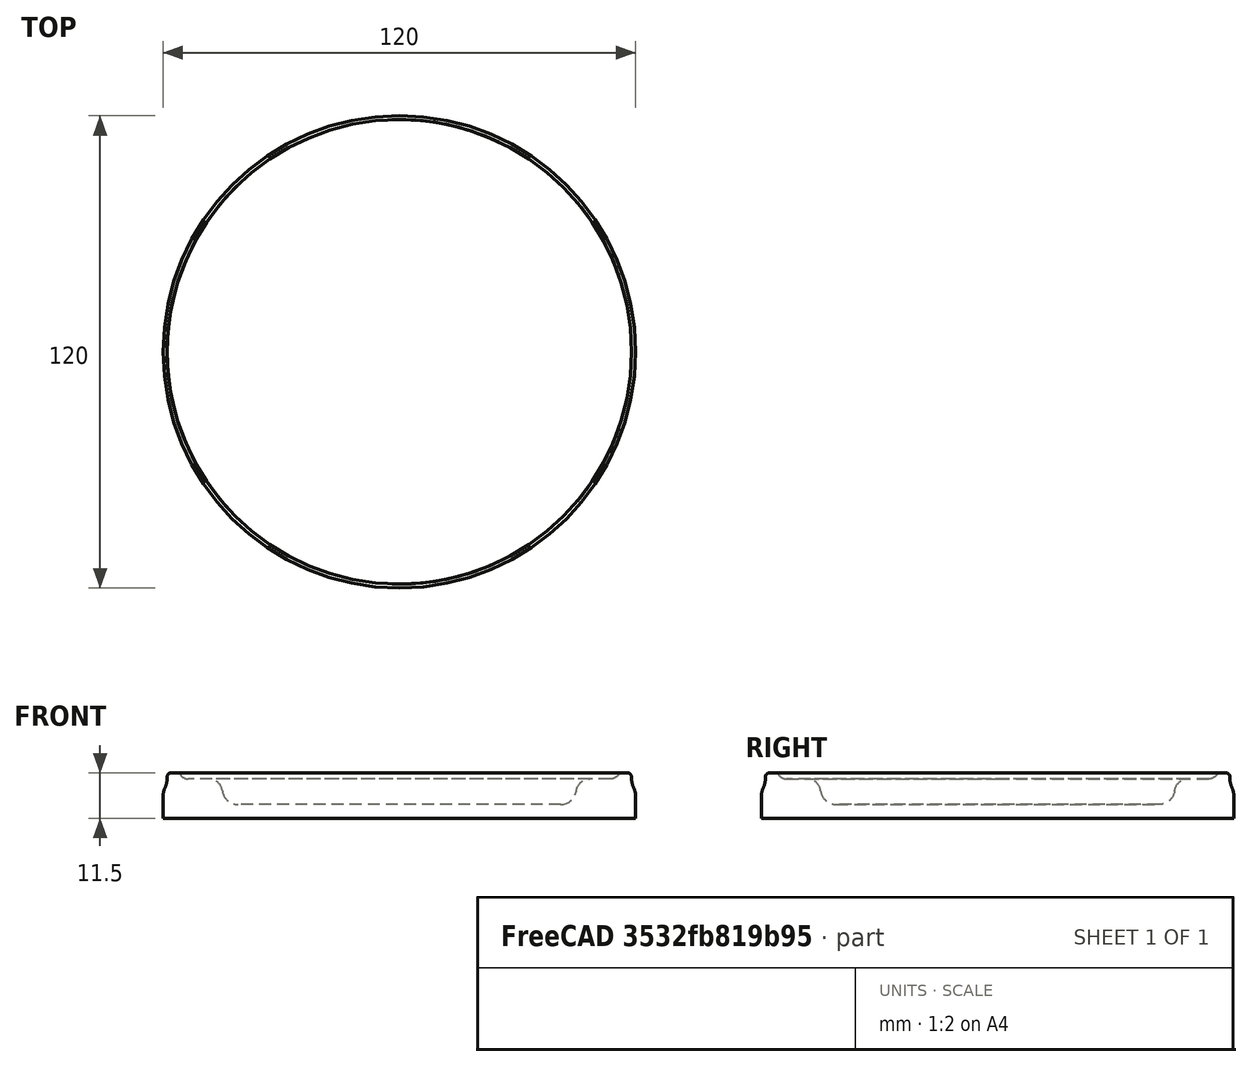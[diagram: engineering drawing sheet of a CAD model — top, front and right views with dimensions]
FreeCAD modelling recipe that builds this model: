
FCSTD DOCUMENT  (FreeCAD 0.16R)
Label: posavasos2017
License: All rights reserved
LicenseURL: http://en.wikipedia.org/wiki/All_rights_reserved
objects: Part::Fillet×6, Part::Cylinder×4, Part::Cut×2, Part::MultiFuse×1
note: 13 computed .brp shape members not serialized (recipe doc carries the construction recipe); baked Part::Feature solids carry a one-line shape summary decoded from their .brp

FEATURE [Part::Cylinder] Cylinder  label="Cilindro"
  Angle = 360
  Height = 30
  Placement = pos=(0,0,3.5) rot=(0,0,1;0rad)
  Radius = 45
FEATURE [Part::Cylinder] Cylinder001  label="Cilindro001"
  Angle = 360
  Height = 10
  Radius = 60
FEATURE [Part::Cut] Cut
  Base = -> Cylinder001
  Tool = -> Cylinder
FEATURE [Part::Fillet] Fillet
  Base = -> Cut
  Edges = 1 edges r=4: [Edge6]
FEATURE [Part::Fillet] Fillet001
  Base = -> Fillet
  Edges = 1 edges r=3.5: [Edge3]
FEATURE [Part::Fillet] Fillet002
  Base = -> Fillet001
  Edges = 1 edges r=4.2: [Edge6]
FEATURE [Part::Cylinder] Cylinder002  label="Cilindro002"
  Angle = 360
  Height = 11
  Radius = 59
FEATURE [Part::Cylinder] Cylinder003  label="Cilindro003"
  Angle = 360
  Height = 20
  Placement = pos=(0,0,-5) rot=(0,0,1;0rad)
  Radius = 55.5
FEATURE [Part::Cut] Cut001
  Base = -> Cylinder002
  Placement = pos=(0,0,1) rot=(0,0,1;0rad)
  Tool = -> Cylinder003
FEATURE [Part::Fillet] Fillet003
  Base = -> Cut001
  Edges = 2 edges r=1: [Edge1,Edge4]
  Placement = pos=(0,0,-0.5) rot=(0,0,1;0rad)
FEATURE [Part::MultiFuse] Fusion
  Shapes = -> [Fillet003,Fillet002]
FEATURE [Part::Fillet] Fillet004
  Base = -> Fusion
  Edges = 1 edges r=2.5: [Edge13]
FEATURE [Part::Fillet] Fillet005
  Base = -> Fillet004
  Edges = 1 edges r=6: [Edge12]
